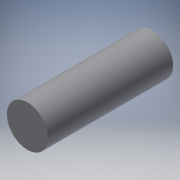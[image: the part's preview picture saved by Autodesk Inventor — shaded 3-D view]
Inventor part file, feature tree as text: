
AUTODESK INVENTOR PART (.ipt)
format: ipt  version: 2019 (Build 230136000, 136)  size: 91,136 bytes
history: native  units: in
note: dims shown in document units (in); Inventor stores cm internally (conversion verified against a paired STEP export)
features: extrude x1, sketch x1
ambient origin geometry x8: Origin, YZ Plane, XZ Plane, XY Plane, X Axis, Y Axis, Z Axis, Center Point
bodies: Solid1 (feature_tree)
feature tree (2):
  extrude  "Extrusion1"  Depth=1.0in TaperAngle=0.0deg
  sketch  "Sketch1"  dims[d0=0.3287in d1=1.0in d2=0.0in]
